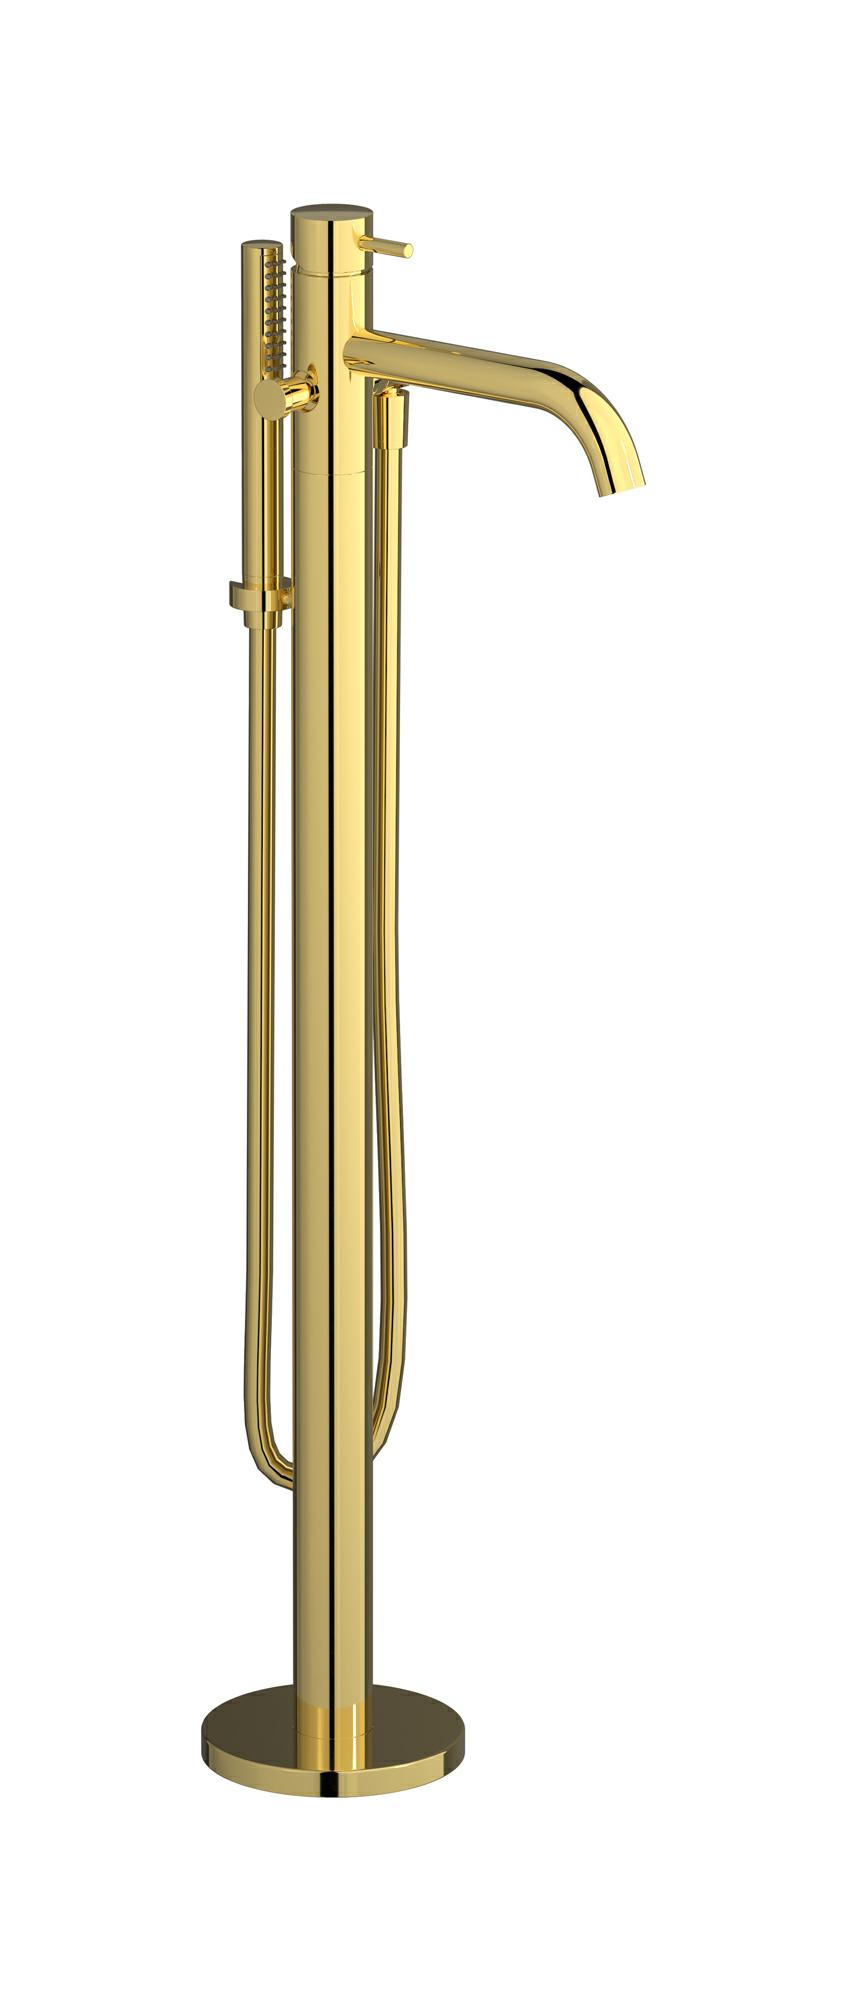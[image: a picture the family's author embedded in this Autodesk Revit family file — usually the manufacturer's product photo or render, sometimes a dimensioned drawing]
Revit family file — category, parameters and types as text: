
# Revit family: MT399
name_source: partatom
category: Apparecchi idraulici
units: mm (PartAtom-declared; Revit-internal decimal feet)

## family parameters
Basato su piano di lavoro = No
Condiviso = No
Mantieni orientamento annotazione = No
Numero OmniClass = 23.45.55.17
Punto di calcolo locali = No
Quota connettore circolare = Usa diametro
Sempre verticale = Sì
Taglio con vuoti quando caricato = No
Tipo di parte = Normale
Titolo OmniClass = Mixing Faucets

## types (13) — shared parameters
Cold water inlet = 10 mm  [stored 0.0328084 ft]
Commenti sul tipo = Freestanding bath filler
Connessione CW = No
Connessione HW = No
Connessione di scarico = No
Connessione di ventilazione = No
Descrizione = Freestanding bath filler
Hot water flow = 0,0 L/s
Hot water inlet = 10 mm  [stored 0.0328084 ft]
Produttore = IB Rubinetterie S.p.A.
URL = https://www.weareib.it
zero-valued in all types: Prospetto di default

## per-type parameters (varying)
| type | Finishes surface | Immagine tipo | Modello |
| Chrome | IB_Chrome | MT399CC.jpg | MT399CC |
| Brushed nickel | IB_Brushed nickel | MT399SS.jpg | MT399SS |
| Matt black | IB_matt black | MT399NP.jpg | MT399NP |
| Matt white | IB_matt white | MT399BO.jpg | MT399BO |
| Natural brass | IB_Brass | MT399ON.jpg | MT399ON |
| Black chrome | IB_Black chrome | MT399CF.jpg | MT399CF |
| Brushed black chrome | IB_Brushed black chrome | MT399CS.jpg | MT399CS |
| Pale gold | IB_Pale gold | MT399II.jpg | MT399II |
| Brushed pale gold | IB_brushed pale gold | MT399IS.jpg | MT399IS |
| Rose gold | IB_Rose gold | MT399RS.jpg | MT399RS |
| Brushed rose gold | IB_Brushed rose gold | MT399SR.jpg | MT399SR |
| Gold | IB_gold | MT399OO.jpg | MT399OO |
| Brushed gold | IB_brushed gold | MT399OS.jpg | MT399OS |

note: [stored X ft] marks values corroborated as IEEE doubles in the binary element streams (Revit-internal decimal feet)
